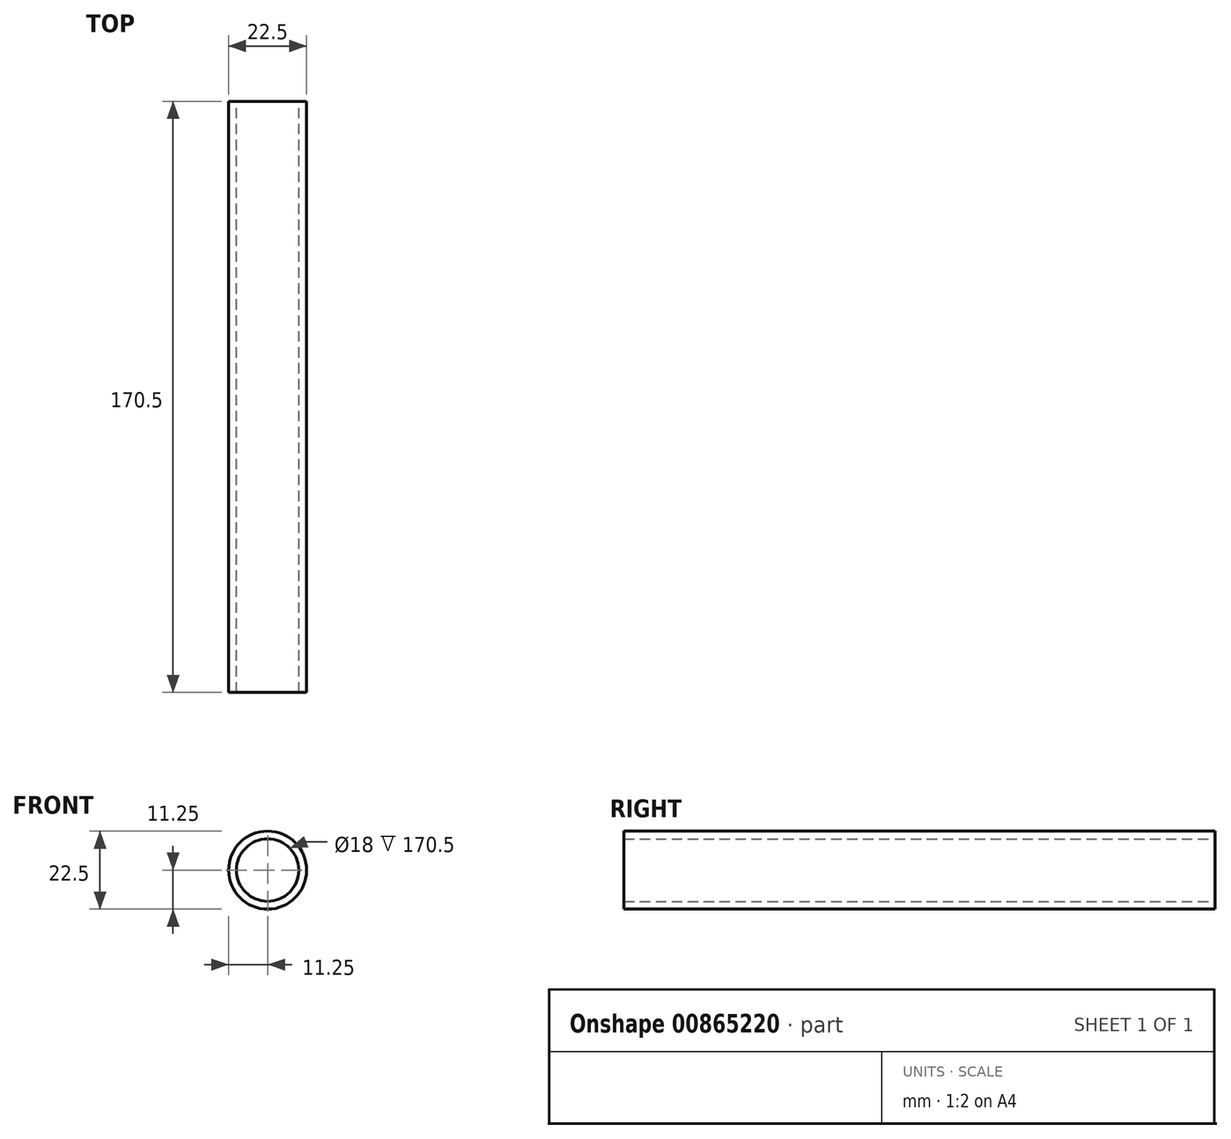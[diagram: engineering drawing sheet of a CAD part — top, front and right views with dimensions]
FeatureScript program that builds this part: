
annotation { "Feature Type Name" : "Feature", "Feature Type Description" : "" }
export const myFeature = defineFeature(function(context is Context, id is Id, definition is map)
    precondition{}
    {
        {
            var Q0;
            Q0=qCreatedBy(makeId("Front.planeOp"),FACE);
            var sketch = newSketch(context, id + "F0", { "sketchPlane" : qUnion([Q0])});
            skCircle(sketch, "E0", {"center": v(0, 0) * mm, "radius": 11.25 * mm});
            skCircle(sketch, "E1", {"center": v(0, 0) * mm, "radius": 9 * mm});
            skSolve(sketch);
        }
        {
            var Q0;
            Q0 = qSketchRegion(id + "F0", true);
            extrude(context, id + "F1", {"entities" : qUnion([Q0]), "depth" : 170.5 * mm, "offsetDistance" : 25 * mm});
        }
    });
